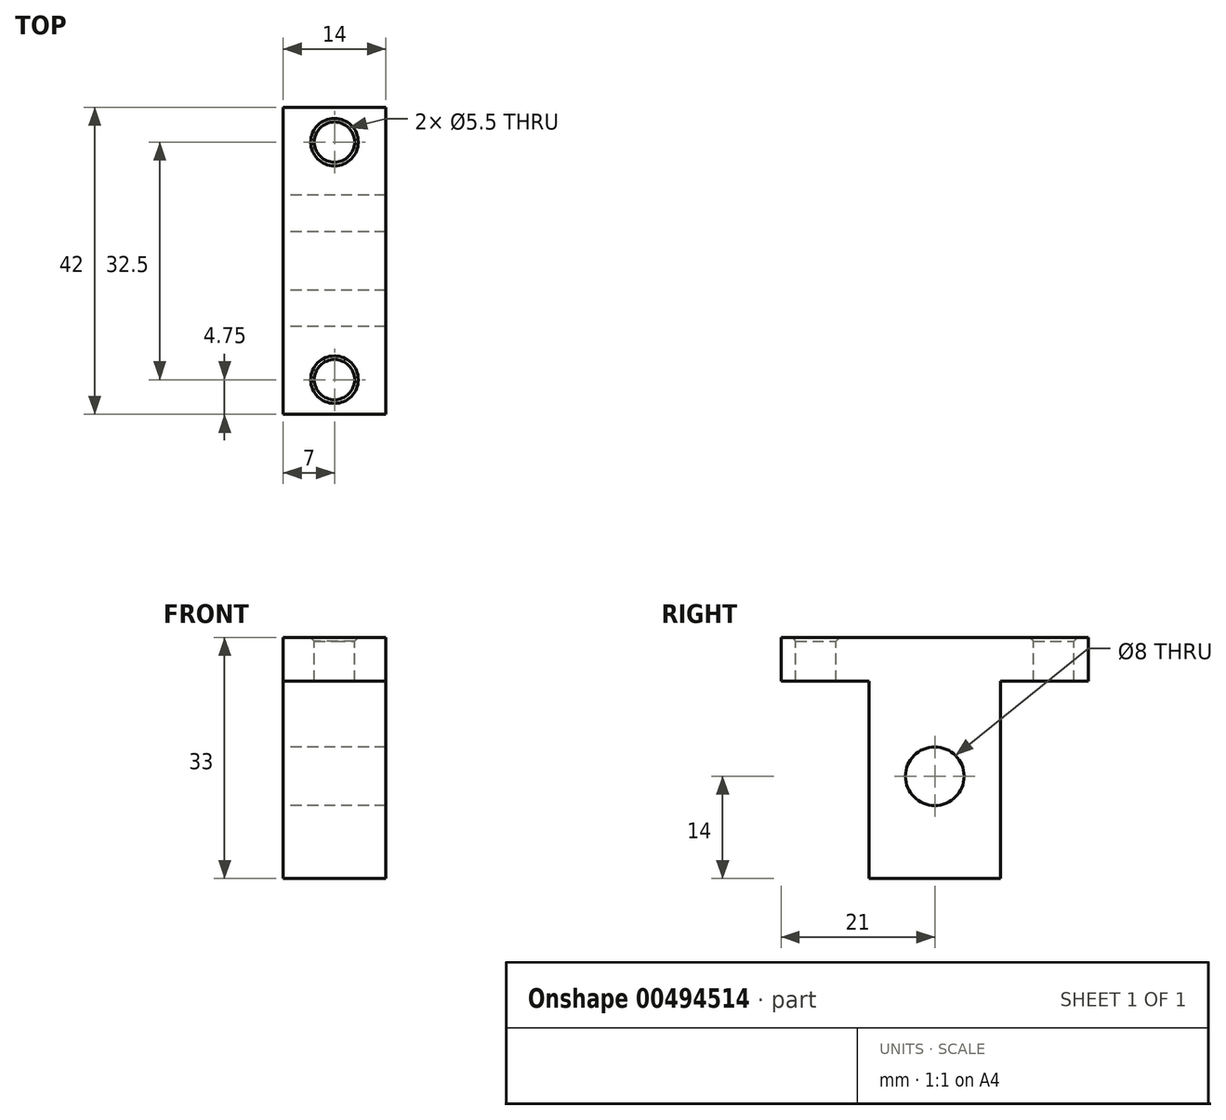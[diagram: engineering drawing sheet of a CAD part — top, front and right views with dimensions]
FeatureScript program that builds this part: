
annotation { "Feature Type Name" : "Feature", "Feature Type Description" : "" }
export const myFeature = defineFeature(function(context is Context, id is Id, definition is map)
    precondition{}
    {
        {
            var Q0;
            Q0=qCreatedBy(makeId("Right.planeOp"),FACE);
            var sketch = newSketch(context, id + "F0", { "sketchPlane" : qUnion([Q0])});
            skCircle(sketch, "E0", {"center": v(0, 0) * mm, "radius": 4 * mm});
            skLineSegment(sketch, "E1", {"start": v(0, 0) * mm, "end": v(0, -19) * mm, "construction": true});
            skLineSegment(sketch, "E2", {"start": v(0, -19) * mm, "end": v(-21, -19) * mm});
            skLineSegment(sketch, "E3", {"start": v(-21, -19) * mm, "end": v(-21, -13) * mm});
            skLineSegment(sketch, "E4", {"start": v(-21, -13) * mm, "end": v(-9, -13) * mm});
            skLineSegment(sketch, "E5", {"start": v(-9, -13) * mm, "end": v(-9, 14) * mm});
            skLineSegment(sketch, "E6", {"start": v(-9, 14) * mm, "end": v(0, 14) * mm});
            skLineSegment(sketch, "E7", {"start": v(0, 0) * mm, "end": v(0, 14) * mm, "construction": true});
            skLineSegment(sketch, "E8.MirrorCS", {"start": v(0, -19) * mm, "end": v(21, -19) * mm});
            skLineSegment(sketch, "E9.MirrorCS", {"start": v(21, -19) * mm, "end": v(21, -13) * mm});
            skLineSegment(sketch, "E10.MirrorCS", {"start": v(21, -13) * mm, "end": v(9, -13) * mm});
            skLineSegment(sketch, "E11.MirrorCS", {"start": v(9, -13) * mm, "end": v(9, 14) * mm});
            skLineSegment(sketch, "E12.MirrorCS", {"start": v(9, 14) * mm, "end": v(0, 14) * mm});
            skSolve(sketch);
        }
        {
            var Q0;
            Q0=makeQuery(id+"F0.imprint","IMPRINT",FACE,{"disambiguationData":[TD([[makeQuery(id+"F0.imprint","IMPRINT",EDGE,{"derivedFrom":sQuery(id+"F0.wireOp",EDGE,"E0")}),-1.0]])]});
            extrude(context, id + "F1", {"entities" : qUnion([Q0]), "depth" : 14 * mm});
        }
        {
            var Q0;
            Q0=makeQuery(id+"F1.opExtrude","SWEPT_BODY",BODY,{"disambiguationData":[OSD([sQuery(id+"F0.wireOp",EDGE,"E0"),sQuery(id+"F0.wireOp",EDGE,"E2"),sQuery(id+"F0.wireOp",EDGE,"E3"),sQuery(id+"F0.wireOp",EDGE,"E4"),sQuery(id+"F0.wireOp",EDGE,"E5"),sQuery(id+"F0.wireOp",EDGE,"E6"),sQuery(id+"F0.wireOp",EDGE,"E8.MirrorCS"),sQuery(id+"F0.wireOp",EDGE,"E9.MirrorCS"),sQuery(id+"F0.wireOp",EDGE,"E10.MirrorCS"),sQuery(id+"F0.wireOp",EDGE,"E11.MirrorCS"),sQuery(id+"F0.wireOp",EDGE,"E12.MirrorCS")])]});
            var Q1;
            Q1=makeQuery(id+"F1.opExtrude","SWEPT_FACE",FACE,{"disambiguationData":[OSD([sQuery(id+"F0.wireOp",EDGE,"E0")])]});
            transform(context, id + "F2", {"entities" : qUnion([Q0]), "transformType" : TransformType.ROTATION, "transformAxis" : qUnion([Q1]), "angle" : 180 * degree, "makeCopy" : false});
        }
        {
            var Q0;
            Q0=makeQuery(id+"F1.opExtrude","SWEPT_FACE",FACE,{"disambiguationData":[OSD([sQuery(id+"F0.wireOp",EDGE,"E2"),sQuery(id+"F0.wireOp",EDGE,"E8.MirrorCS")])]});
            var sketch = newSketch(context, id + "F3", { "sketchPlane" : qUnion([Q0])});
            skPoint(sketch, "E13", {"position": v(7, -16.25) * mm});
            skPoint(sketch, "E13.positionSnap0", {"position": v(7, -21) * mm});
            skLineSegment(sketch, "E14", {"start": v(14, 0) * mm, "end": v(0, 0) * mm, "construction": true});
            skPoint(sketch, "E15.MirrorP", {"position": v(7, 16.25) * mm});
            skSolve(sketch);
        }
        {
            var Q0;
            Q0=sQuery(id+"F3.wireOp",VERTEX,"E13");
            var Q1;
            Q1=sQuery(id+"F3.wireOp",VERTEX,"E15.MirrorP");
            var Q2;
            Q2=makeQuery(id+"F1.opExtrude","SWEPT_BODY",BODY,{"disambiguationData":[OSD([sQuery(id+"F0.wireOp",EDGE,"E0"),sQuery(id+"F0.wireOp",EDGE,"E2"),sQuery(id+"F0.wireOp",EDGE,"E3"),sQuery(id+"F0.wireOp",EDGE,"E4"),sQuery(id+"F0.wireOp",EDGE,"E5"),sQuery(id+"F0.wireOp",EDGE,"E6"),sQuery(id+"F0.wireOp",EDGE,"E8.MirrorCS"),sQuery(id+"F0.wireOp",EDGE,"E9.MirrorCS"),sQuery(id+"F0.wireOp",EDGE,"E10.MirrorCS"),sQuery(id+"F0.wireOp",EDGE,"E11.MirrorCS"),sQuery(id+"F0.wireOp",EDGE,"E12.MirrorCS")])]});
            hole(context, id + "F4", {"style" : HoleStyle.C_SINK, "endStyle" : HoleEndStyle.THROUGH, "holeDiameter" : 5.5 * mm, "cSinkDiameter" : 6.5 * mm, "cSinkAngle" : 90 * degree, "locations" : qUnion([Q0, Q1]), "scope" : qUnion([Q2]), "isTappedThrough" : true});
        }
    });
